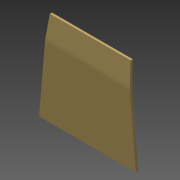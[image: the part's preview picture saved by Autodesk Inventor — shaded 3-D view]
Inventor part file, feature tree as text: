
AUTODESK INVENTOR PART (.ipt)
format: ipt  version: 2015 (Build 190159000, 159)  size: 106,496 bytes
history: native  units: mm
features: sketch x3, other x2, loft x1
ambient origin geometry x8: Origin, YZ Plane, XZ Plane, XY Plane, X Axis, Y Axis, Z Axis, Center Point
bodies: Body1 (feature_tree)
feature tree (6):
  sketch  "Szkic1"
  other  "Płaszczyzna konstrukcyjna2"
  loft  "Wyciągnięcie złożone1"
  other  "Gięcie części1"
  sketch  "Szkic3"
  sketch  "Szkic4"
